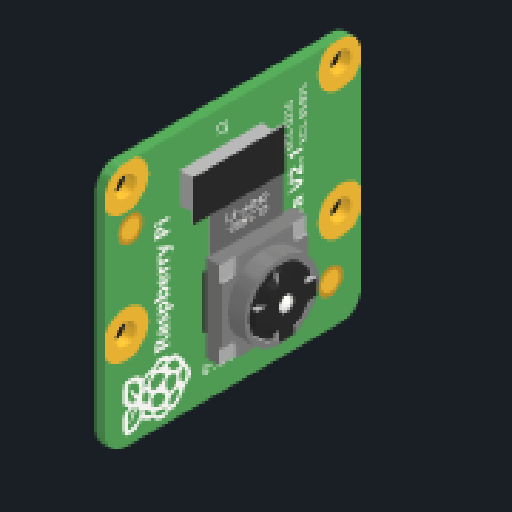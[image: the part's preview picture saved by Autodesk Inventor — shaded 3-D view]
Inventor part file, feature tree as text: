
AUTODESK INVENTOR PART (.ipt)
format: ipt  version: 2023 (Build 270158000, 158)  size: 2,803,712 bytes
history: native  units: mm
features: sketch x3, other x2, plane x2, projected_geometry x1
ambient origin geometry x8: Origin, YZ Plane, XZ Plane, XY Plane, X Axis, Y Axis, Z Axis, Center Point
bodies: Solid1 (feature_tree), Body1 (feature_tree)
feature tree (8):
  other  "Decal1"
  plane  "Work Plane1"
  sketch  "Sketch2"  dims[d52=150.0mm]
  plane  "Work Plane2"
  sketch  "Sketch3"  dims[d54=4.258603mm d55=5.427974mm]
  sketch  "Sketch1"  dims[d45=0.0mm]
  other  "Image1"
  projected_geometry  "Projected Loop1"
